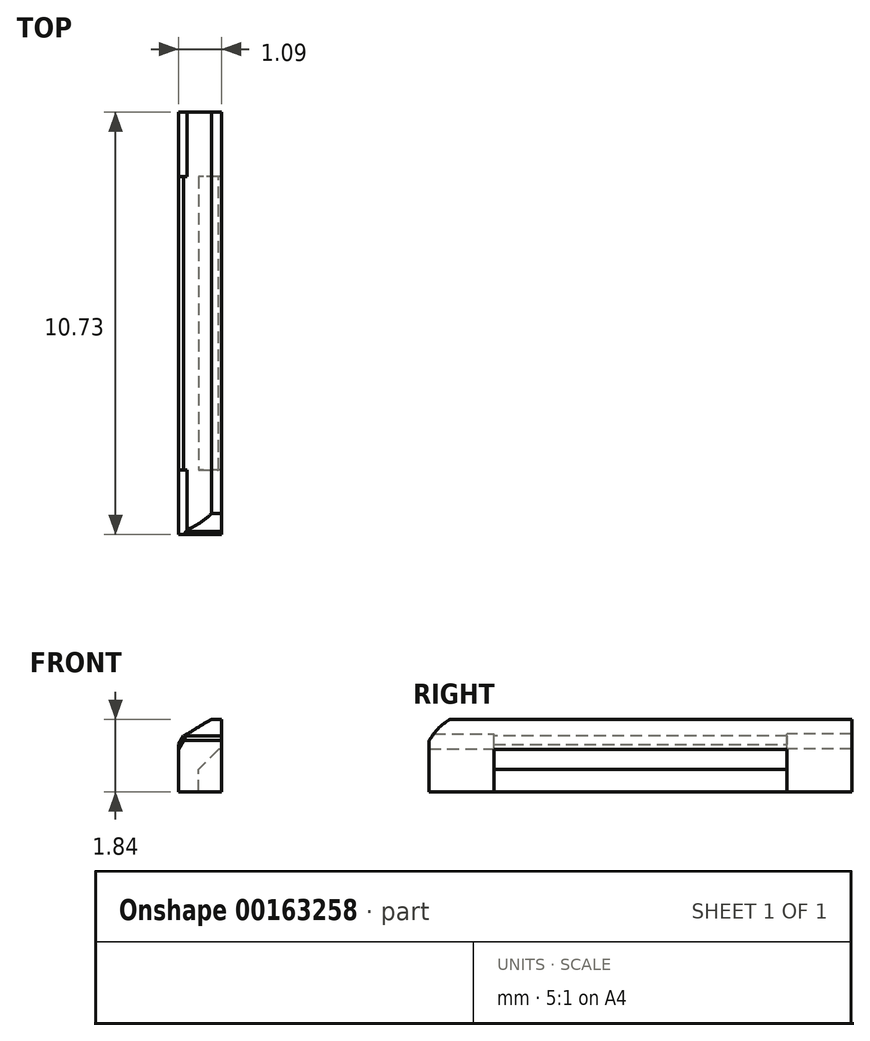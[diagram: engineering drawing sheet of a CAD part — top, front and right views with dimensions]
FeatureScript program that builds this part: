
annotation { "Feature Type Name" : "Feature", "Feature Type Description" : "" }
export const myFeature = defineFeature(function(context is Context, id is Id, definition is map)
    precondition{}
    {
        {
            var Q0;
            Q0=qCreatedBy(makeId("Front.planeOp"),FACE);
            var sketch = newSketch(context, id + "F0", { "sketchPlane" : qUnion([Q0])});
            skLineSegment(sketch, "E0.bottom", {"start": v(0, 0) * mm, "end": v(1.1, 0) * mm});
            skLineSegment(sketch, "E0.left", {"start": v(0, 0) * mm, "end": v(0, 1.34) * mm});
            skLineSegment(sketch, "E0.right", {"start": v(1.1, 0) * mm, "end": v(1.1, 1.09) * mm});
            skLineSegment(sketch, "E1", {"start": v(0, 1.34) * mm, "end": v(1.1, 2) * mm});
            skLineSegment(sketch, "E2", {"start": v(1.1, 2) * mm, "end": v(1.1, 1.09) * mm});
            skSolve(sketch);
        }
        {
            var Q0;
            Q0 = qSketchRegion(id + "F0", true);
            extrude(context, id + "F1", {"entities" : qUnion([Q0]), "depth" : 7.45 * mm});
        }
        {
            var Q0;
            Q0=makeQuery(id+"F1.opExtrude","CAP_FACE",FACE,{"disambiguationData":[OSD([sQuery(id+"F0.wireOp",EDGE,"E0.bottom"),sQuery(id+"F0.wireOp",EDGE,"E0.left"),sQuery(id+"F0.wireOp",EDGE,"E0.right"),sQuery(id+"F0.wireOp",EDGE,"E1"),sQuery(id+"F0.wireOp",EDGE,"E2")])],"isStart":false});
            var sketch = newSketch(context, id + "F2", { "sketchPlane" : qUnion([Q0])});
            skLineSegment(sketch, "E3.bottom", {"start": v(1.1, 0) * mm, "end": v(0.51, 0) * mm});
            skLineSegment(sketch, "E3.top", {"start": v(1.1, 1.07) * mm, "end": v(0.51, 1.07) * mm});
            skLineSegment(sketch, "E3.left", {"start": v(1.1, 0) * mm, "end": v(1.1, 1.07) * mm});
            skLineSegment(sketch, "E3.right", {"start": v(0.51, 0) * mm, "end": v(0.51, 1.07) * mm});
            skSolve(sketch);
        }
        {
            var Q0;
            Q0 = qSketchRegion(id + "F2", true);
            extrude(context, id + "F3", {"entities" : qUnion([Q0]), "operationType" : NewBodyOperationType.REMOVE, "endBound" : BoundingType.THROUGH_ALL, "oppositeDirection" : true, "depth" : 25 * mm});
        }
        {
            var Q0;
            Q0=makeQuery(id+"F3.boolean.opBoolean","COPY",EDGE,{"derivedFrom":makeQuery(id+"F3.opExtrude","SWEPT_EDGE",EDGE,{"disambiguationData":[OSD([sQuery(id+"F2.wireOp",EDGE,"E3.top"),sQuery(id+"F2.wireOp",EDGE,"E3.right")])]})});
            chamfer(context, id + "F4", {"entities" : qUnion([Q0]), "width" : .5 * mm, "tangentPropagation" : true});
        }
        {
            var Q0;
            Q0=makeQuery(id+"F1.opExtrude","SWEPT_EDGE",EDGE,{"disambiguationData":[OSD([sQuery(id+"F0.wireOp",EDGE,"E0.left"),sQuery(id+"F0.wireOp",EDGE,"E1")])]});
            chamfer(context, id + "F5", {"entities" : qUnion([Q0]), "width" : .25 * mm, "tangentPropagation" : true});
        }
        {
            var Q0;
            Q0=makeQuery(id+"F1.opExtrude","CAP_FACE",FACE,{"disambiguationData":[OSD([sQuery(id+"F0.wireOp",EDGE,"E0.bottom"),sQuery(id+"F0.wireOp",EDGE,"E0.left"),sQuery(id+"F0.wireOp",EDGE,"E0.right"),sQuery(id+"F0.wireOp",EDGE,"E1"),sQuery(id+"F0.wireOp",EDGE,"E2")])],"isStart":true});
            var sketch = newSketch(context, id + "F6", { "sketchPlane" : qUnion([Q0])});
            skLineSegment(sketch, "E4", {"start": v(-1.1, 2) * mm, "end": v(-1.1, 0) * mm});
            skLineSegment(sketch, "E5", {"start": v(-1.1, 0) * mm, "end": v(0, 0) * mm});
            skLineSegment(sketch, "E6", {"start": v(0, 0) * mm, "end": v(0, 1.1) * mm});
            skLineSegment(sketch, "E7", {"start": v(0, 1.1) * mm, "end": v(-0.21, 1.47) * mm});
            skLineSegment(sketch, "E8", {"start": v(-0.21, 1.47) * mm, "end": v(-1.1, 2) * mm});
            skSolve(sketch);
        }
        {
            var Q0;
            Q0 = qSketchRegion(id + "F6", true);
            extrude(context, id + "F7", {"entities" : qUnion([Q0]), "operationType" : NewBodyOperationType.ADD, "depth" : ((2 - 1.45 / 2) + 0.37) * mm});
        }
        {
            var Q0;
            Q0=makeQuery(id+"F1.opExtrude","CAP_FACE",FACE,{"disambiguationData":[OSD([sQuery(id+"F0.wireOp",EDGE,"E0.bottom"),sQuery(id+"F0.wireOp",EDGE,"E0.left"),sQuery(id+"F0.wireOp",EDGE,"E0.right"),sQuery(id+"F0.wireOp",EDGE,"E1"),sQuery(id+"F0.wireOp",EDGE,"E2")])],"isStart":false});
            var sketch = newSketch(context, id + "F8", { "sketchPlane" : qUnion([Q0])});
            skLineSegment(sketch, "E9", {"start": v(1.1, 2) * mm, "end": v(1.1, 0) * mm});
            skLineSegment(sketch, "E10", {"start": v(1.1, 0) * mm, "end": v(0, 0) * mm});
            skLineSegment(sketch, "E11", {"start": v(0, 0) * mm, "end": v(0, 1.1) * mm});
            skLineSegment(sketch, "E12", {"start": v(0, 1.1) * mm, "end": v(0.21, 1.47) * mm});
            skLineSegment(sketch, "E13", {"start": v(0.21, 1.47) * mm, "end": v(1.1, 2) * mm});
            skSolve(sketch);
        }
        {
            var Q0;
            Q0 = qSketchRegion(id + "F8", true);
            extrude(context, id + "F9", {"entities" : qUnion([Q0]), "operationType" : NewBodyOperationType.ADD, "depth" : ((2 - 1.45 / 2) + 0.37) * mm});
        }
        {
            var Q0;
            Q0=makeQuery(id+"F9.boolean.opBoolean","MERGE",FACE,{"derivedFrom":[makeQuery(id+"F7.boolean.opBoolean","MERGE",FACE,{"derivedFrom":[makeQuery(id+"F1.opExtrude","SWEPT_FACE",FACE,{"disambiguationData":[OSD([sQuery(id+"F0.wireOp",EDGE,"E0.right"),sQuery(id+"F0.wireOp",EDGE,"E2")])]}),makeQuery(id+"F7.opExtrude","SWEPT_FACE",FACE,{"disambiguationData":[OSD([sQuery(id+"F6.wireOp",EDGE,"E4")])]})]}),makeQuery(id+"F9.opExtrude","SWEPT_FACE",FACE,{"disambiguationData":[OSD([sQuery(id+"F8.wireOp",EDGE,"E9")])]})]});
            var sketch = newSketch(context, id + "F10", { "sketchPlane" : qUnion([Q0])});
            skLineSegment(sketch, "E14", {"start": v(-9.1, 1.31) * mm, "end": v(-9, 1.42) * mm});
            skArc(sketch, "E15", {"start": v(-7.62, 2) * mm, "mid": v(-8.4, 1.92) * mm, "end": v(-9, 1.42) * mm});
            skLineSegment(sketch, "E16", {"start": v(-9.1, 1.31) * mm, "end": v(-9.1, 2) * mm});
            skLineSegment(sketch, "E17", {"start": v(-9.1, 2) * mm, "end": v(-7.62, 2) * mm});
            skSolve(sketch);
        }
        {
            var Q0;
            Q0=makeQuery(id+"F9.boolean.opBoolean","MERGE",FACE,{"derivedFrom":[makeQuery(id+"F7.boolean.opBoolean","MERGE",FACE,{"derivedFrom":[makeQuery(id+"F1.opExtrude","SWEPT_FACE",FACE,{"disambiguationData":[OSD([sQuery(id+"F0.wireOp",EDGE,"E0.right"),sQuery(id+"F0.wireOp",EDGE,"E2")])]}),makeQuery(id+"F7.opExtrude","SWEPT_FACE",FACE,{"disambiguationData":[OSD([sQuery(id+"F6.wireOp",EDGE,"E4")])]})]}),makeQuery(id+"F9.opExtrude","SWEPT_FACE",FACE,{"disambiguationData":[OSD([sQuery(id+"F8.wireOp",EDGE,"E9")])]})]});
            var sketch = newSketch(context, id + "F11", { "sketchPlane" : qUnion([Q0])});
            skLineSegment(sketch, "E18.bottom", {"start": v(1.64, 2) * mm, "end": v(-9.1, 2) * mm});
            skLineSegment(sketch, "E18.top", {"start": v(1.64, 1.84) * mm, "end": v(-9.1, 1.84) * mm});
            skLineSegment(sketch, "E18.left", {"start": v(1.64, 2) * mm, "end": v(1.64, 1.84) * mm});
            skLineSegment(sketch, "E18.right", {"start": v(-9.1, 2) * mm, "end": v(-9.1, 1.84) * mm});
            skSolve(sketch);
        }
        {
            var Q0;
            Q0 = qSketchRegion(id + "F11", true);
            extrude(context, id + "F12", {"entities" : qUnion([Q0]), "operationType" : NewBodyOperationType.REMOVE, "endBound" : BoundingType.THROUGH_ALL, "oppositeDirection" : true, "depth" : 25 * mm});
        }
        {
            var Q0;
            Q0 = qSketchRegion(id + "F10", true);
            extrude(context, id + "F13", {"entities" : qUnion([Q0]), "operationType" : NewBodyOperationType.REMOVE, "endBound" : BoundingType.THROUGH_ALL, "oppositeDirection" : true, "depth" : 25 * mm});
        }
    });
